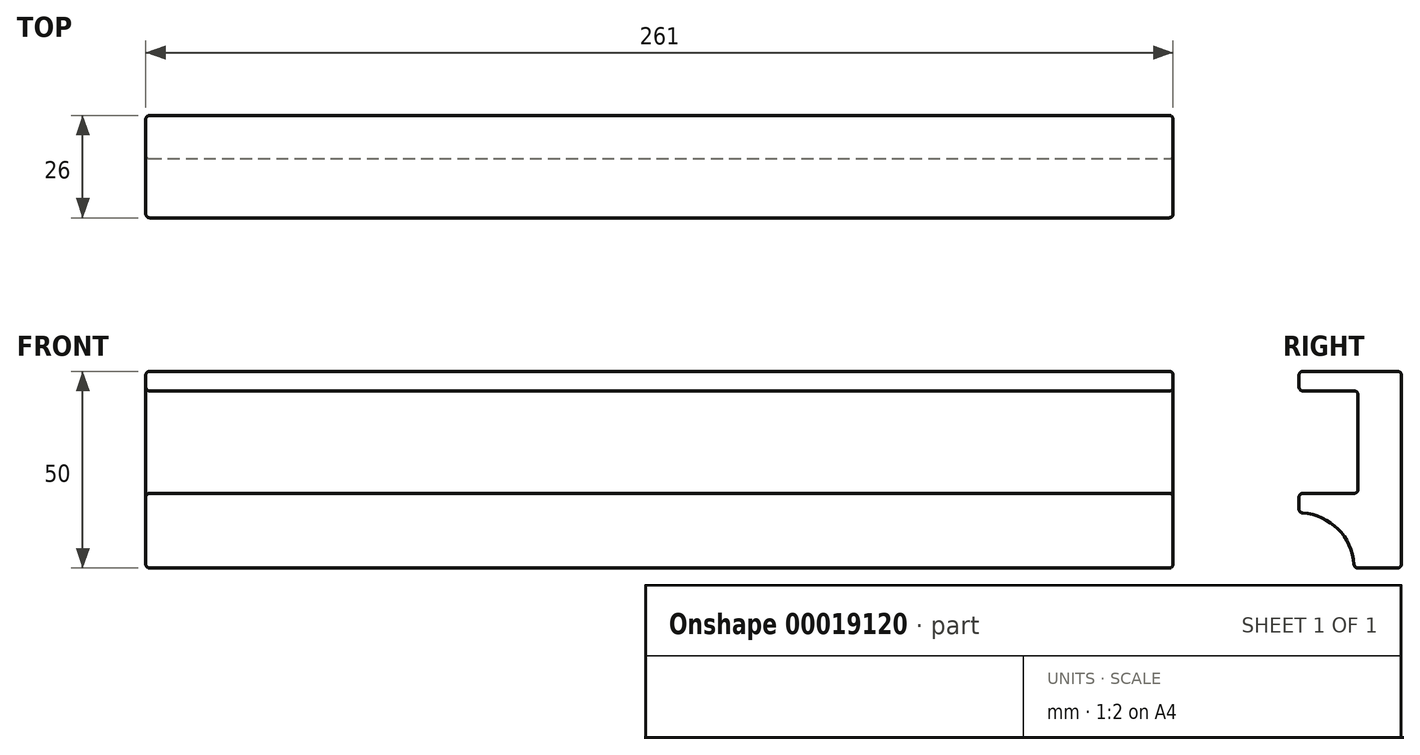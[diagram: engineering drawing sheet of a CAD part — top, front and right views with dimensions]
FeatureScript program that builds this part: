
annotation { "Feature Type Name" : "Feature", "Feature Type Description" : "" }
export const myFeature = defineFeature(function(context is Context, id is Id, definition is map)
    precondition{}
    {
        {
            var Q0;
            Q0=qCreatedBy(makeId("Front.planeOp"),FACE);
            var sketch = newSketch(context, id + "F0", { "sketchPlane" : qUnion([Q0])});
            skLineSegment(sketch, "E0.bottom", {"start": v(0, 0) * mm, "end": v(261, 0) * mm});
            skLineSegment(sketch, "E0.top", {"start": v(0, -50) * mm, "end": v(261, -50) * mm});
            skLineSegment(sketch, "E0.left", {"start": v(0, 0) * mm, "end": v(0, -50) * mm});
            skLineSegment(sketch, "E0.right", {"start": v(261, 0) * mm, "end": v(261, -50) * mm});
            skSolve(sketch);
        }
        {
            var Q0;
            Q0=makeQuery(id+"F0.imprint","IMPRINT",FACE,{"disambiguationData":[TD([[makeQuery(id+"F0.imprint","IMPRINT",EDGE,{"derivedFrom":sQuery(id+"F0.wireOp",EDGE,"E0.bottom")}),-1.0]])]});
            extrude(context, id + "F1", {"entities" : qUnion([Q0]), "depth" : 26 * mm});
        }
        {
            var Q0;
            Q0=makeQuery(id+"F1.opExtrude","SWEPT_FACE",FACE,{"disambiguationData":[OSD([sQuery(id+"F0.wireOp",EDGE,"E0.right")])]});
            var sketch = newSketch(context, id + "F2", { "sketchPlane" : qUnion([Q0])});
            skLineSegment(sketch, "E1", {"start": v(-26, 0) * mm, "end": v(-26, -5) * mm});
            skLineSegment(sketch, "E2", {"start": v(-26, -5) * mm, "end": v(-11, -5) * mm});
            skLineSegment(sketch, "E3", {"start": v(-11, -5) * mm, "end": v(-11, -31) * mm});
            skLineSegment(sketch, "E4", {"start": v(-11, -31) * mm, "end": v(-26, -31) * mm});
            skLineSegment(sketch, "E5", {"start": v(-26, -31) * mm, "end": v(-26, -36) * mm});
            skArc(sketch, "E6", {"start": v(-12, -50.25) * mm, "mid": v(-16.01, -40.19) * mm, "end": v(-26, -36) * mm});
            skSolve(sketch);
        }
        {
            var Q0;
            {var subQ2=sQuery(id+"F2.wireOp",EDGE,"E2");Q0=makeQuery(id+"F2.imprint","IMPRINT",FACE,{"disambiguationData":[TD([[makeQuery(id+"F2.imprint","IMPRINT",EDGE,{"derivedFrom":subQ2}),-1.0]])]});}
            var Q1;
            {var subQ0=sQuery(id+"F0.wireOp",EDGE,"E0.right");var subQ1=makeQuery(id+"F1.opExtrude","CAP_EDGE",EDGE,{"disambiguationData":[OSD([subQ0])],"isStart":false});var subQ2=sQuery(id+"F2.wireOp",EDGE,"E6");var subQ3=makeQuery(id+"F2.imprint","INTERSECT",VERTEX,{"derivedFrom":[subQ1,sQuery(id+"F2.wireOp",EDGE,"E5"),subQ2]});Q1=makeQuery(id+"F2.imprint","IMPRINT",FACE,{"disambiguationData":[TD([[makeQuery(id+"F2.imprint","IMPRINT",EDGE,{"disambiguationData":[TD([[subQ3,1.0]])],"derivedFrom":subQ2}),1.0]])]});}
            extrude(context, id + "F3", {"entities" : qUnion([Q0, Q1]), "operationType" : NewBodyOperationType.REMOVE, "endBound" : BoundingType.THROUGH_ALL, "oppositeDirection" : true, "depth" : 25 * mm});
        }
        {
            var Q0;
            Q0=makeQuery(id+"F1.opExtrude","SWEPT_FACE",FACE,{"disambiguationData":[OSD([sQuery(id+"F0.wireOp",EDGE,"E0.bottom")])]});
            var Q1;
            Q1=makeQuery(id+"F1.opExtrude","SWEPT_FACE",FACE,{"disambiguationData":[OSD([sQuery(id+"F0.wireOp",EDGE,"E0.left")])]});
            var Q2;
            Q2=makeQuery(id+"F3.boolean.opBoolean","COPY",FACE,{"derivedFrom":makeQuery(id+"F3.opExtrude","SWEPT_FACE",FACE,{"disambiguationData":[OSD([sQuery(id+"F2.wireOp",EDGE,"E3")])]})});
            var Q3;
            Q3=makeQuery(id+"F3.boolean.opBoolean","COPY",EDGE,{"derivedFrom":makeQuery(id+"F3.opExtrude","SWEPT_EDGE",EDGE,{"disambiguationData":[OSD([sQuery(id+"F0.wireOp",EDGE,"E0.right"),sQuery(id+"F2.wireOp",EDGE,"E1"),sQuery(id+"F2.wireOp",EDGE,"E2")])]})});
            var Q4;
            {var subQ0=sQuery(id+"F0.wireOp",EDGE,"E0.left");var subQ1=sQuery(id+"F0.wireOp",EDGE,"E0.right");Q4=makeQuery(id+"F3.boolean.opBoolean","SPLIT",FACE,{"disambiguationData":[TD([makeQuery(id+"F3.opExtrude","SWEPT_FACE",FACE,{"disambiguationData":[OSD([sQuery(id+"F2.wireOp",EDGE,"E4")])]})])],"derivedFrom":makeQuery(id+"F1.opExtrude","CAP_FACE",FACE,{"disambiguationData":[OSD([sQuery(id+"F0.wireOp",EDGE,"E0.bottom"),sQuery(id+"F0.wireOp",EDGE,"E0.top"),subQ0,subQ1])],"isStart":false})});}
            var Q5;
            Q5=makeQuery(id+"F3.boolean.opBoolean","COPY",EDGE,{"derivedFrom":makeQuery(id+"F3.opExtrude","SWEPT_EDGE",EDGE,{"disambiguationData":[OSD([sQuery(id+"F0.wireOp",EDGE,"E0.top"),sQuery(id+"F0.wireOp",EDGE,"E0.right"),sQuery(id+"F2.wireOp",EDGE,"E6")])]})});
            var Q6;
            Q6=makeQuery(id+"F1.opExtrude","CAP_FACE",FACE,{"disambiguationData":[OSD([sQuery(id+"F0.wireOp",EDGE,"E0.bottom"),sQuery(id+"F0.wireOp",EDGE,"E0.top"),sQuery(id+"F0.wireOp",EDGE,"E0.left"),sQuery(id+"F0.wireOp",EDGE,"E0.right")])],"isStart":true});
            var Q7;
            Q7=makeQuery(id+"F1.opExtrude","SWEPT_FACE",FACE,{"disambiguationData":[OSD([sQuery(id+"F0.wireOp",EDGE,"E0.top")])]});
            var Q8;
            Q8=makeQuery(id+"F1.opExtrude","SWEPT_FACE",FACE,{"disambiguationData":[OSD([sQuery(id+"F0.wireOp",EDGE,"E0.right")])]});
            fillet(context, id + "F4", {"entities" : qUnion([Q0, Q1, Q2, Q3, Q4, Q5, Q6, Q7, Q8]), "radius" : 1 * mm, "tangentPropagation" : true, "allowEdgeOverflow" : false});
        }
    });
